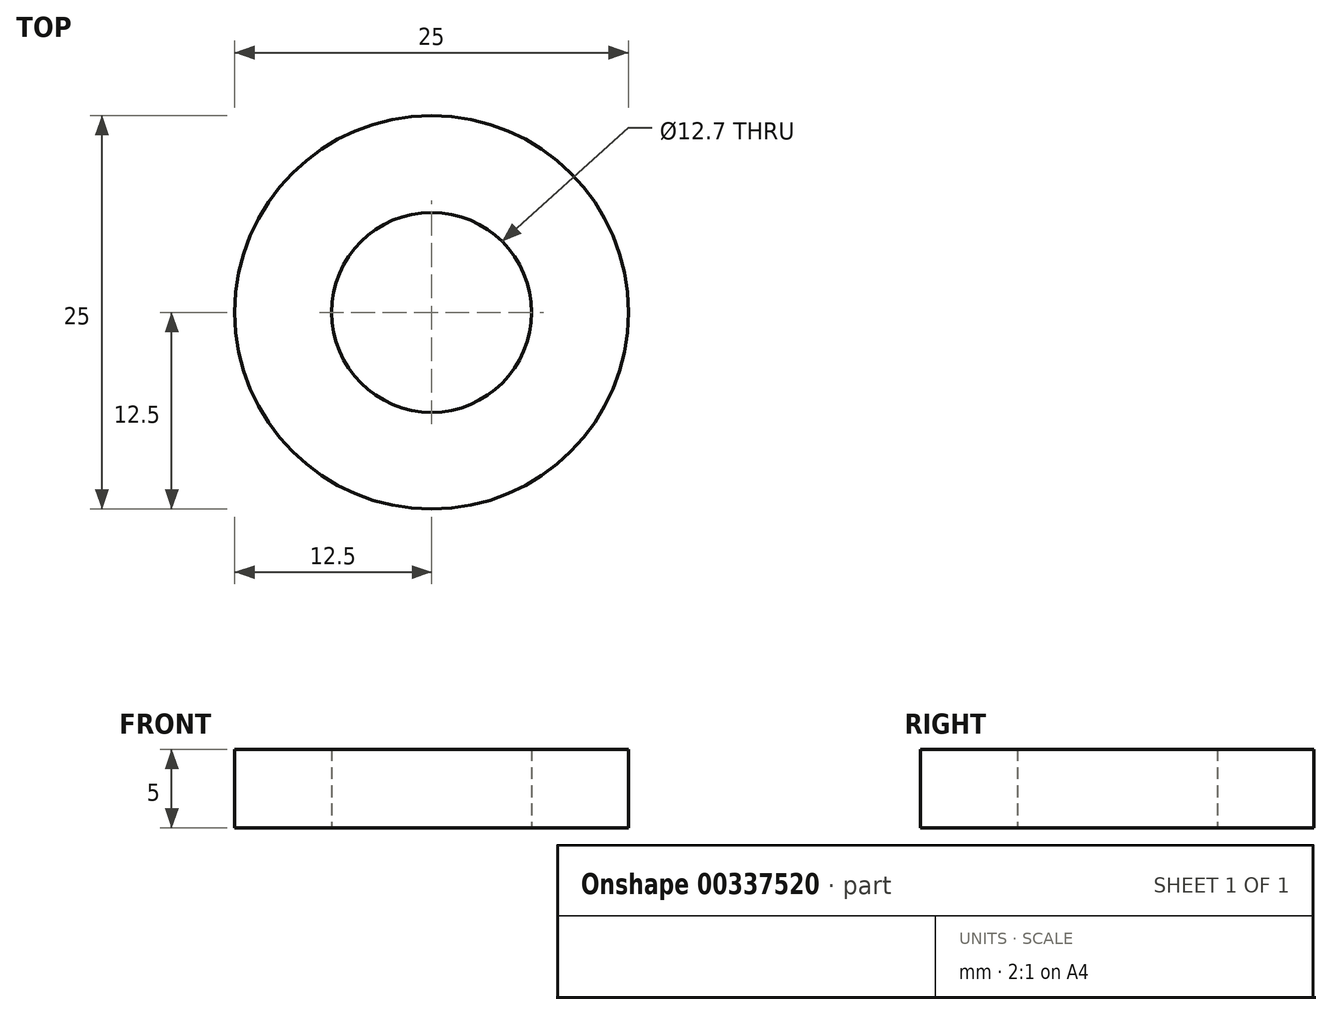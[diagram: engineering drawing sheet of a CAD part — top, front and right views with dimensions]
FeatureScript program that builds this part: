
annotation { "Feature Type Name" : "Feature", "Feature Type Description" : "" }
export const myFeature = defineFeature(function(context is Context, id is Id, definition is map)
    precondition{}
    {
        {
            var Q0;
            Q0=qCreatedBy(makeId("Top.planeOp"),FACE);
            var sketch = newSketch(context, id + "F0", { "sketchPlane" : qUnion([Q0])});
            skCircle(sketch, "E0", {"center": v(0, 0) * mm, "radius": 12.5 * mm});
            skCircle(sketch, "E1", {"center": v(0, 0) * mm, "radius": 6.35 * mm});
            skSolve(sketch);
        }
        {
            var Q0;
            Q0=makeQuery(id+"F0.imprint","IMPRINT",FACE,{"disambiguationData":[TD([[makeQuery(id+"F0.imprint","IMPRINT",EDGE,{"derivedFrom":sQuery(id+"F0.wireOp",EDGE,"E0")}),1.0]])]});
            extrude(context, id + "F1", {"entities" : qUnion([Q0]), "depth" : 5 * mm});
        }
    });
